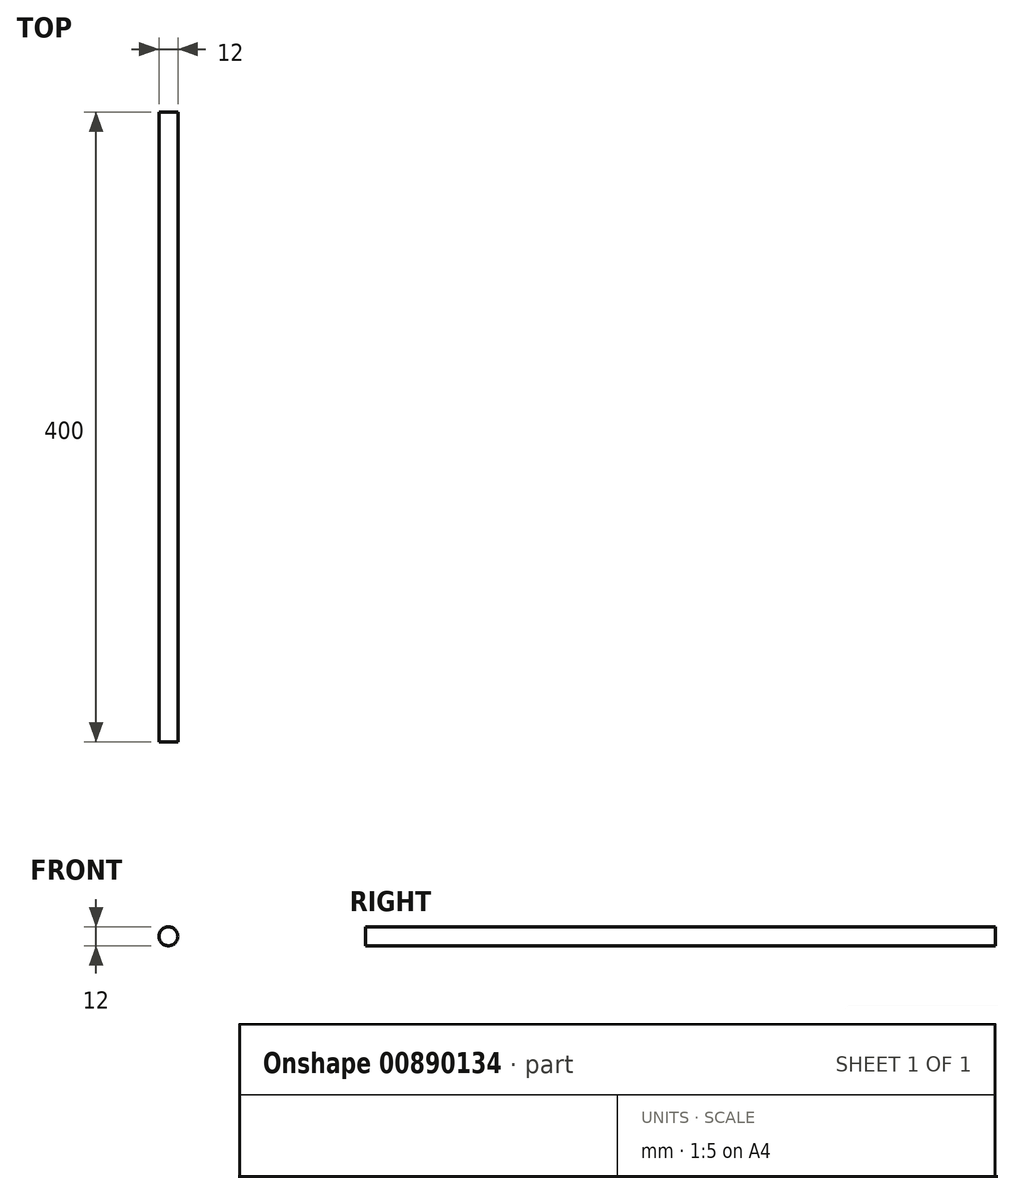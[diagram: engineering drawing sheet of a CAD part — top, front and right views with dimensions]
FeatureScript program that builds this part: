
annotation { "Feature Type Name" : "Feature", "Feature Type Description" : "" }
export const myFeature = defineFeature(function(context is Context, id is Id, definition is map)
    precondition{}
    {
        {
            var Q0;
            Q0=qCreatedBy(makeId("Front.planeOp"),FACE);
            var sketch = newSketch(context, id + "F0", { "sketchPlane" : qUnion([Q0])});
            skCircle(sketch, "E0", {"center": v(0, 0) * mm, "radius": 6 * mm});
            skSolve(sketch);
        }
        {
            var Q0;
            Q0=qSketchRegion(id+"F0",true);
            extrude(context, id + "F1", {"entities" : qUnion([Q0]), "depth" : 400 * mm, "offsetDistance" : 25 * mm});
        }
    });
